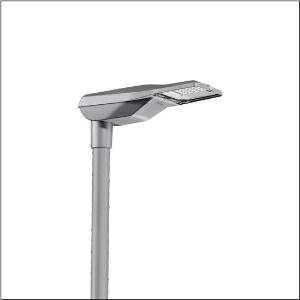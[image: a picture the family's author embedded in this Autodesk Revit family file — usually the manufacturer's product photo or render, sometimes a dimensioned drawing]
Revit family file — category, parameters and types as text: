
# Revit family: streetlight_sl_21_micro___st1_0a_5xe5d43a08db_2c1a
name_source: partatom
category: Lighting Fixtures
units: mm (PartAtom-declared; Revit-internal decimal feet)

## family parameters
Cut with Voids When Loaded = No
Host = Face
Light Source = No
Part Type = Normal
Room Calculation Point = No
Round Connector Dimension = Use Diameter
Shared = No

## types (1)
- --- (1 x LED, 5320 lm, 39.1 W, 4000K)
    Apparent Load = 39 VA
    CIE Flux Codes = 37 72 97 100 100
    Color Rendering = 70
    Color Temperature = 4000K
    Default Elevation = 1800 mm
    Description = Streetlight SL 21 micro, mast luminaire, primary light control with lens, of PMMA, primary optical cover: cover, of toughened safety glass, transparent, light distribution: ST1.0a, light emission: direct distribution, primary light characteristic: asymmetric, installation type: side-entry, post-top, LED, 3G 1.5mm², High Power LED, rated luminous flux: 5.320lm, luminous efficacy: 136lm/W, light colour: 740, colour temperature: 4000K, control: flexible luminous flux parameterisation, time-dependent luminous flux control, constant luminous flux control, overheat protection, mains connection: 230..240V, AC, 50/60Hz, connection cable pre-assembled, cable length: 6,5m, wiring characteristics: H07RN-F, start of lifetime: 39W, end of service life: 41W, reduction: 18W, luminaire housing, of diecast aluminium, powder-coated, Siteco® metallic grey (DB 702S), corrosivity category C5 mid according to DIN EN ISO 12944, please order mast flange separately, inclination adjustable: 0°, 5°, 10°, 15°, sealing non-destructively replaceable, multi-level sealing system, length: 528mm, width: 235mm, height: 110mm, mast flange for spigot size: 42mm (side-entry): 5XC10008XM4, 60/48mm (side-entry/post-top): 5XC10108XM2, 76/60mm (side-entry/post-top): 5XC10108XM1, protection rating (complete): IP66, insulation class (complete): insulation class II (safety insulation), certification: CE, ENEC, ENEC+, VDE, impact resistance: IK09, permissible operating ambient temperature for outdoor applications: -40..+50°C, standard-compliant lighting for roads and squares, packaging unit: 1 piece

Light Distribution: ST1.0a
    Height = 110 mm
    Lamp = 1 x LED
    Lamp Light Flux = 5320 lm
    Lamp Power = 39.1 W
    Lamp count = 1
    Length = 528 mm
    Luminous efficacy = 136 lm/W
    Manufacturer = Siteco
    ModVariant = No
    Model = 5XE5D43A08DB
    Number of Poles = 1
    OnlyDefault = Yes
    Power Factor = 1
    Product Name = Streetlight SL 21 micro | ST1.0a
    Product group = mast luminaire | pylon top
    ProductGroupID = 6100
    Protection Class = Protection class II
    Protection Degree = IP 66
    RLX_Detail_Level = 1
    RLX_Emergency_Light_Flux = 0 lm
    RLX_Emergency_Type = 0
    RLX_Emergency_Type_DB = No
    RlxData = <blob elided: 99021 chars, md5=91c63a31>
    Socket = socket
    Standby Power = 0 W
    System Light Flux = 5320 lm
    System Power = 39 W
    Type Comments = factory setting: luminous flux: 100 % | Output Level: 100 % | 765 mA
    Type Image = l_1006881.jpg
    URL = http://relux.com
    VarID = @adj_125937
    Voltage = 0 V
    Weight = 0.00 kg
    Width = 235 mm

## geometry (parser evidence)
native form markers: Blend x4, Sweep x11
no freeform markers — native parametric forms only
